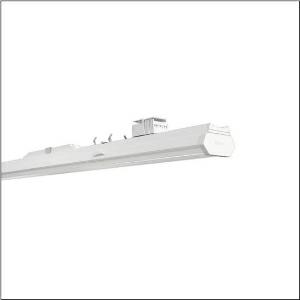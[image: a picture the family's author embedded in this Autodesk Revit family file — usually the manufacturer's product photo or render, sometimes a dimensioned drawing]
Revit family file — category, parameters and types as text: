
# Revit family: licross_r__11_protected_mo_51td12vn465f_59e7
name_source: partatom
category: Lighting Fixtures
units: mm (PartAtom-declared; Revit-internal decimal feet)

## family parameters
Cut with Voids When Loaded = No
Host = Face
Light Source = No
Part Type = Normal
Room Calculation Point = No
Round Connector Dimension = Use Diameter
Shared = No

## types (1)
- --- (1 x LED, 6510 lm, 40.1 W, 4000K)
    Apparent Load = 40 VA
    CIE Flux Codes = 73 92 98 99 100
    Color Rendering = 80
    Color Temperature = 4000K
    Default Elevation = 1800 mm
    Description = Licross® 11 Protected MO, luminaire insert, of sheet steel, galvanised, coil coated, white, length: 1.500mm, width: 90mm, height: 101mm, LED rated luminous flux: 6.510lm, light colour: 840, control gear: DALI 2, CLO, control gear: ECG DALI, with plug, 5-pole, with phase selection, mains connection: 220..240V, AC, 50/60Hz, halogen-free wiring, primary optical cover: cover, of PMMA, light emission: direct with ceiling illumination distribution, protection rating (complete): IP54, insulation class (complete): insulation class I (protective earthing), certification: CE, ENEC, VDE, UKCA, protection symbol: D if used in an environment with non-conductive dust loads with corresponding accessories, permissible ambient temperature for indoor applications: -25..+40°C, corresponds to IFS (International Featured Standards) requirements for safety and quality in the food industry, reducing of maximum allowable ambient temperature of 5°C with ceiling mounting, LABS conformity tested according to VDMA 24364:2018-05, packaging unit: 1 piece
    Height = 92 mm
    Lamp = 1 x LED
    Lamp Light Flux = 6510 lm
    Lamp Power = 40.1 W
    Lamp count = 1
    Length = 1500 mm
    Luminous efficacy = 162 lm/W
    Manufacturer = Siteco
    ModVariant = No
    Model = 51TD12VN465F
    Mounting Place = Ceiling
    Mounting Type = Pendant
    Number of Poles = 1
    OnlyDefault = Yes
    Power Factor = 1
    Product Name = Licross® 11 Protected MO
    Product group = luminaire insert
    ProductGroupID = 902
    Protection Class = Protection class I
    Protection Degree = IP 54
    RLX_Detail_Level = 1
    RlxData = <blob elided: 24269 chars, md5=03c7e4ef>
    Socket = socket
    Standby Power = 0 W
    System Light Flux = 6510 lm
    System Power = 40 W
    Type Comments = factory setting: luminous flux: 100 % | dim-lin: 254 | 264 mA
    Type Image = l_1256145.jpg
    URL = http://relux.com
    VarID = @adj_060663
    Voltage = 0 V
    Weight = 0.00 kg
    Width = 88 mm

## geometry (parser evidence)
native form markers: Blend x4, Sweep x12
no freeform markers — native parametric forms only
